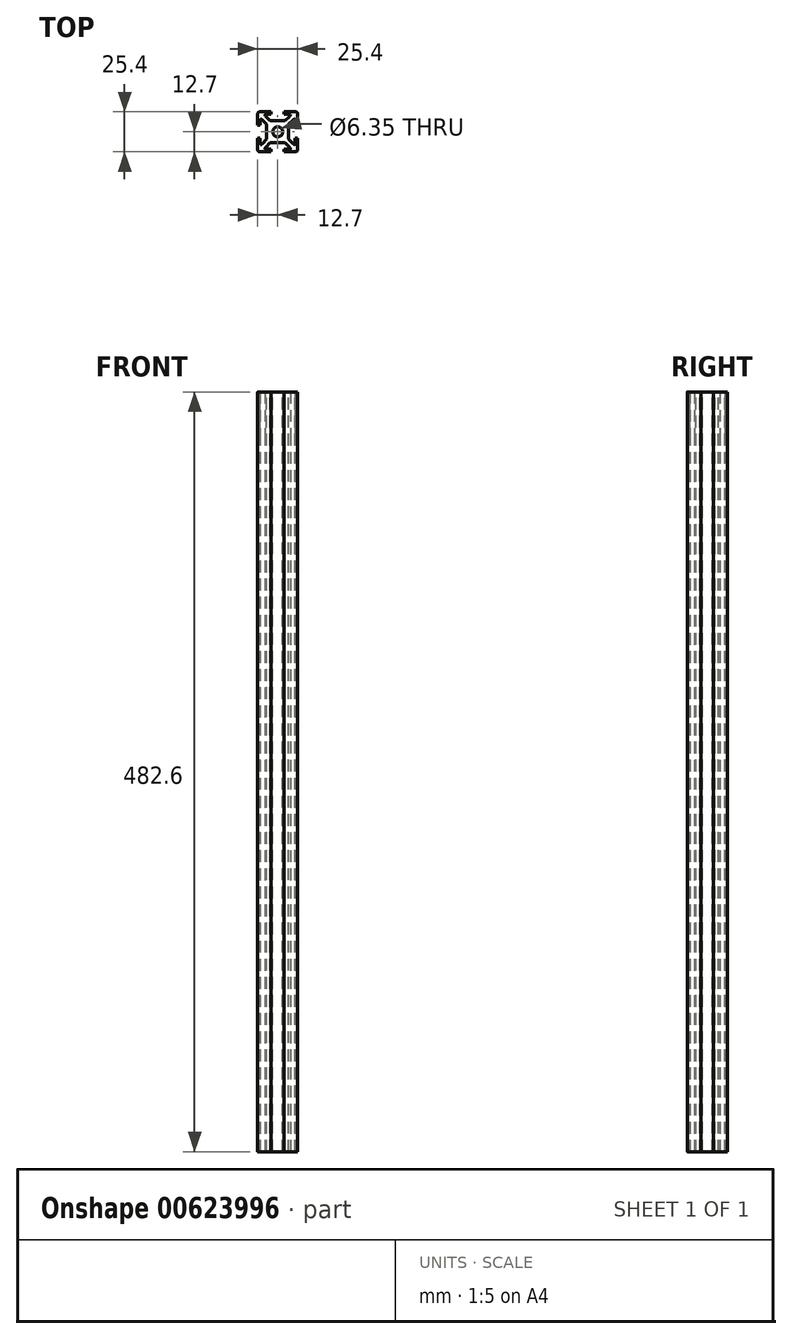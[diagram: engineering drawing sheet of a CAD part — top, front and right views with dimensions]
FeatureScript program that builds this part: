
annotation { "Feature Type Name" : "Feature", "Feature Type Description" : "" }
export const myFeature = defineFeature(function(context is Context, id is Id, definition is map)
    precondition{}
    {
        {
            var Q0;
            Q0=qCreatedBy(makeId("Top.planeOp"),FACE);
            var sketch = newSketch(context, id + "F0", { "sketchPlane" : qUnion([Q0])});
            skLineSegment(sketch, "E0.bottom", {"start": v(12.7, 12.7) * mm, "end": v(-12.7, 12.7) * mm});
            skLineSegment(sketch, "E0.top", {"start": v(12.7, -12.7) * mm, "end": v(-12.7, -12.7) * mm});
            skLineSegment(sketch, "E0.left", {"start": v(12.7, 12.7) * mm, "end": v(12.7, -12.7) * mm});
            skLineSegment(sketch, "E0.right", {"start": v(-12.7, 12.7) * mm, "end": v(-12.7, -12.7) * mm});
            skPoint(sketch, "E0.middle", {"position": v(0, 0) * mm});
            skSolve(sketch);
        }
        {
            var Q0;
            Q0=makeQuery(id+"F0.imprint","IMPRINT",FACE,{"disambiguationData":[TD([[makeQuery(id+"F0.imprint","IMPRINT",EDGE,{"derivedFrom":sQuery(id+"F0.wireOp",EDGE,"E0.bottom")}),1.0]])]});
            extrude(context, id + "F1", {"entities" : qUnion([Q0]), "depth" : 455.93 * mm, "offsetDistance" : 25.4 * mm});
        }
        {
            var Q0;
            Q0=makeQuery(id+"F1.opExtrude","CAP_FACE",FACE,{"disambiguationData":[OSD([sQuery(id+"F0.wireOp",EDGE,"E0.bottom"),sQuery(id+"F0.wireOp",EDGE,"E0.top"),sQuery(id+"F0.wireOp",EDGE,"E0.left"),sQuery(id+"F0.wireOp",EDGE,"E0.right")])],"isStart":false});
            var sketch = newSketch(context, id + "F2", { "sketchPlane" : qUnion([Q0])});
            skLineSegment(sketch, "E1", {"start": v(-7, 4.76) * mm, "end": v(-7, -4.76) * mm});
            skLineSegment(sketch, "E2", {"start": v(-7, -4.76) * mm, "end": v(-11.11, -8.87) * mm});
            skLineSegment(sketch, "E3", {"start": v(-11.11, -8.87) * mm, "end": v(-11.11, -4.1) * mm});
            skLineSegment(sketch, "E4", {"start": v(-11.11, -4.1) * mm, "end": v(-12.7, -4.1) * mm});
            skLineSegment(sketch, "E5", {"start": v(-12.7, -4.1) * mm, "end": v(-12.7, 4.1) * mm});
            skLineSegment(sketch, "E6", {"start": v(-12.7, 4.1) * mm, "end": v(-11.11, 4.1) * mm});
            skLineSegment(sketch, "E7", {"start": v(-11.11, 4.1) * mm, "end": v(-11.11, 8.87) * mm});
            skLineSegment(sketch, "E8", {"start": v(-11.11, 8.87) * mm, "end": v(-7, 4.76) * mm});
            skLineSegment(sketch, "E9", {"start": v(-4.1, -12.7) * mm, "end": v(-4.1, -11.11) * mm});
            skLineSegment(sketch, "E10", {"start": v(-4.1, -11.11) * mm, "end": v(-8.87, -11.11) * mm});
            skLineSegment(sketch, "E11", {"start": v(-8.87, -11.11) * mm, "end": v(-4.76, -7) * mm});
            skLineSegment(sketch, "E12", {"start": v(-4.76, -7) * mm, "end": v(4.76, -7) * mm});
            skLineSegment(sketch, "E13", {"start": v(4.76, -7) * mm, "end": v(8.87, -11.11) * mm});
            skLineSegment(sketch, "E14", {"start": v(8.87, -11.11) * mm, "end": v(4.1, -11.11) * mm});
            skLineSegment(sketch, "E15", {"start": v(4.1, -11.11) * mm, "end": v(4.1, -12.7) * mm});
            skLineSegment(sketch, "E16", {"start": v(4.1, -12.7) * mm, "end": v(-4.1, -12.7) * mm});
            skLineSegment(sketch, "E17", {"start": v(12.7, -4.1) * mm, "end": v(11.11, -4.1) * mm});
            skLineSegment(sketch, "E18", {"start": v(11.11, -4.1) * mm, "end": v(11.11, -8.87) * mm});
            skLineSegment(sketch, "E19", {"start": v(11.11, -8.87) * mm, "end": v(7, -4.76) * mm});
            skLineSegment(sketch, "E20", {"start": v(7, -4.76) * mm, "end": v(7, 4.76) * mm});
            skLineSegment(sketch, "E21", {"start": v(7, 4.76) * mm, "end": v(11.11, 8.87) * mm});
            skLineSegment(sketch, "E22", {"start": v(11.11, 8.87) * mm, "end": v(11.11, 4.1) * mm});
            skLineSegment(sketch, "E23", {"start": v(11.11, 4.1) * mm, "end": v(12.7, 4.1) * mm});
            skLineSegment(sketch, "E24", {"start": v(12.7, 4.1) * mm, "end": v(12.7, -4.1) * mm});
            skLineSegment(sketch, "E25", {"start": v(-4.1, 12.7) * mm, "end": v(-4.1, 11.11) * mm});
            skLineSegment(sketch, "E26", {"start": v(-4.1, 11.11) * mm, "end": v(-8.87, 11.11) * mm});
            skLineSegment(sketch, "E27", {"start": v(-8.87, 11.11) * mm, "end": v(-4.76, 7) * mm});
            skLineSegment(sketch, "E28", {"start": v(-4.76, 7) * mm, "end": v(4.76, 7) * mm});
            skLineSegment(sketch, "E29", {"start": v(4.76, 7) * mm, "end": v(8.87, 11.11) * mm});
            skLineSegment(sketch, "E30", {"start": v(8.87, 11.11) * mm, "end": v(4.1, 11.11) * mm});
            skLineSegment(sketch, "E31", {"start": v(4.1, 11.11) * mm, "end": v(4.1, 12.7) * mm});
            skLineSegment(sketch, "E32", {"start": v(4.1, 12.7) * mm, "end": v(-4.1, 12.7) * mm});
            skSolve(sketch);
        }
        {
            var Q0;
            Q0=makeQuery(id+"F2.imprint","IMPRINT",FACE,{"disambiguationData":[TD([[makeQuery(id+"F2.imprint","IMPRINT",EDGE,{"derivedFrom":sQuery(id+"F2.wireOp",EDGE,"E1")}),-1.0]])]});
            var Q1;
            Q1=makeQuery(id+"F2.imprint","IMPRINT",FACE,{"disambiguationData":[TD([[makeQuery(id+"F2.imprint","IMPRINT",EDGE,{"derivedFrom":sQuery(id+"F2.wireOp",EDGE,"E25")}),1.0]])]});
            var Q2;
            Q2=makeQuery(id+"F2.imprint","IMPRINT",FACE,{"disambiguationData":[TD([[makeQuery(id+"F2.imprint","IMPRINT",EDGE,{"derivedFrom":sQuery(id+"F2.wireOp",EDGE,"E17")}),-1.0]])]});
            var Q3;
            Q3=makeQuery(id+"F2.imprint","IMPRINT",FACE,{"disambiguationData":[TD([[makeQuery(id+"F2.imprint","IMPRINT",EDGE,{"derivedFrom":sQuery(id+"F2.wireOp",EDGE,"E9")}),-1.0]])]});
            extrude(context, id + "F3", {"entities" : qUnion([Q0, Q1, Q2, Q3]), "operationType" : NewBodyOperationType.REMOVE, "oppositeDirection" : true, "depth" : 455.93 * mm, "offsetDistance" : 25.4 * mm});
        }
        {
            var Q0;
            Q0=makeQuery(id+"F1.opExtrude","CAP_FACE",FACE,{"disambiguationData":[OSD([sQuery(id+"F0.wireOp",EDGE,"E0.bottom"),sQuery(id+"F0.wireOp",EDGE,"E0.top"),sQuery(id+"F0.wireOp",EDGE,"E0.left"),sQuery(id+"F0.wireOp",EDGE,"E0.right")])],"isStart":false});
            var sketch = newSketch(context, id + "F4", { "sketchPlane" : qUnion([Q0])});
            skCircle(sketch, "E33", {"center": v(0, 0) * mm, "radius": 3.18 * mm});
            skSolve(sketch);
        }
        {
            var Q0;
            Q0=makeQuery(id+"F4.imprint","IMPRINT",FACE,{"disambiguationData":[TD([[makeQuery(id+"F4.imprint","IMPRINT",EDGE,{"derivedFrom":sQuery(id+"F4.wireOp",EDGE,"E33")}),1.0]])]});
            extrude(context, id + "F5", {"entities" : qUnion([Q0]), "operationType" : NewBodyOperationType.REMOVE, "oppositeDirection" : true, "depth" : 455.93 * mm, "offsetDistance" : 25.4 * mm});
        }
        {
            var Q0;
            Q0=makeQuery(id+"F1.opExtrude","SWEPT_EDGE",EDGE,{"disambiguationData":[OSD([sQuery(id+"F0.wireOp",EDGE,"E0.bottom"),sQuery(id+"F0.wireOp",EDGE,"E0.right")])]});
            var Q1;
            Q1=makeQuery(id+"F1.opExtrude","SWEPT_EDGE",EDGE,{"disambiguationData":[OSD([sQuery(id+"F0.wireOp",EDGE,"E0.bottom"),sQuery(id+"F0.wireOp",EDGE,"E0.left")])]});
            var Q2;
            Q2=makeQuery(id+"F1.opExtrude","SWEPT_EDGE",EDGE,{"disambiguationData":[OSD([sQuery(id+"F0.wireOp",EDGE,"E0.top"),sQuery(id+"F0.wireOp",EDGE,"E0.left")])]});
            var Q3;
            Q3=makeQuery(id+"F1.opExtrude","SWEPT_EDGE",EDGE,{"disambiguationData":[OSD([sQuery(id+"F0.wireOp",EDGE,"E0.top"),sQuery(id+"F0.wireOp",EDGE,"E0.right")])]});
            fillet(context, id + "F6", {"entities" : qUnion([Q0, Q1, Q2, Q3]), "radius" : 1.59 * mm, "tangentPropagation" : true, "rho" : 0.5, "crossSection" : FilletCrossSection.CONIC, "allowEdgeOverflow" : false});
        }
        {
            var Q0;
            Q0=makeQuery(id+"F3.boolean.opBoolean","COPY",EDGE,{"derivedFrom":makeQuery(id+"F3.opExtrude","SWEPT_EDGE",EDGE,{"disambiguationData":[OSD([sQuery(id+"F2.wireOp",EDGE,"E7"),sQuery(id+"F2.wireOp",EDGE,"E8")])]})});
            var Q1;
            Q1=makeQuery(id+"F3.boolean.opBoolean","COPY",EDGE,{"derivedFrom":makeQuery(id+"F3.opExtrude","SWEPT_EDGE",EDGE,{"disambiguationData":[OSD([sQuery(id+"F2.wireOp",EDGE,"E21"),sQuery(id+"F2.wireOp",EDGE,"E22")])]})});
            var Q2;
            Q2=makeQuery(id+"F3.boolean.opBoolean","COPY",EDGE,{"derivedFrom":makeQuery(id+"F3.opExtrude","SWEPT_EDGE",EDGE,{"disambiguationData":[OSD([sQuery(id+"F2.wireOp",EDGE,"E18"),sQuery(id+"F2.wireOp",EDGE,"E19")])]})});
            var Q3;
            Q3=makeQuery(id+"F3.boolean.opBoolean","COPY",EDGE,{"derivedFrom":makeQuery(id+"F3.opExtrude","SWEPT_EDGE",EDGE,{"disambiguationData":[OSD([sQuery(id+"F2.wireOp",EDGE,"E2"),sQuery(id+"F2.wireOp",EDGE,"E3")])]})});
            var Q4;
            Q4=makeQuery(id+"F3.boolean.opBoolean","COPY",EDGE,{"derivedFrom":makeQuery(id+"F3.opExtrude","SWEPT_EDGE",EDGE,{"disambiguationData":[OSD([sQuery(id+"F2.wireOp",EDGE,"E10"),sQuery(id+"F2.wireOp",EDGE,"E11")])]})});
            var Q5;
            Q5=makeQuery(id+"F3.boolean.opBoolean","COPY",EDGE,{"derivedFrom":makeQuery(id+"F3.opExtrude","SWEPT_EDGE",EDGE,{"disambiguationData":[OSD([sQuery(id+"F2.wireOp",EDGE,"E13"),sQuery(id+"F2.wireOp",EDGE,"E14")])]})});
            var Q6;
            Q6=makeQuery(id+"F3.boolean.opBoolean","COPY",EDGE,{"derivedFrom":makeQuery(id+"F3.opExtrude","SWEPT_EDGE",EDGE,{"disambiguationData":[OSD([sQuery(id+"F2.wireOp",EDGE,"E29"),sQuery(id+"F2.wireOp",EDGE,"E30")])]})});
            var Q7;
            Q7=makeQuery(id+"F3.boolean.opBoolean","COPY",EDGE,{"derivedFrom":makeQuery(id+"F3.opExtrude","SWEPT_EDGE",EDGE,{"disambiguationData":[OSD([sQuery(id+"F2.wireOp",EDGE,"E26"),sQuery(id+"F2.wireOp",EDGE,"E27")])]})});
            fillet(context, id + "F7", {"entities" : qUnion([Q0, Q1, Q2, Q3, Q4, Q5, Q6, Q7]), "radius" : 0.8 * mm, "tangentPropagation" : true, "rho" : 0.5, "crossSection" : FilletCrossSection.CONIC, "allowEdgeOverflow" : false});
        }
        {
            var Q0;
            Q0=makeQuery(id+"F1.opExtrude","CAP_FACE",FACE,{"disambiguationData":[OSD([sQuery(id+"F0.wireOp",EDGE,"E0.bottom"),sQuery(id+"F0.wireOp",EDGE,"E0.top"),sQuery(id+"F0.wireOp",EDGE,"E0.left"),sQuery(id+"F0.wireOp",EDGE,"E0.right")])],"isStart":false});
            extrude(context, id + "F8", {"entities" : qUnion([Q0]), "operationType" : NewBodyOperationType.ADD, "depth" : 26.67 * mm, "offsetDistance" : 25.4 * mm});
        }
    });
